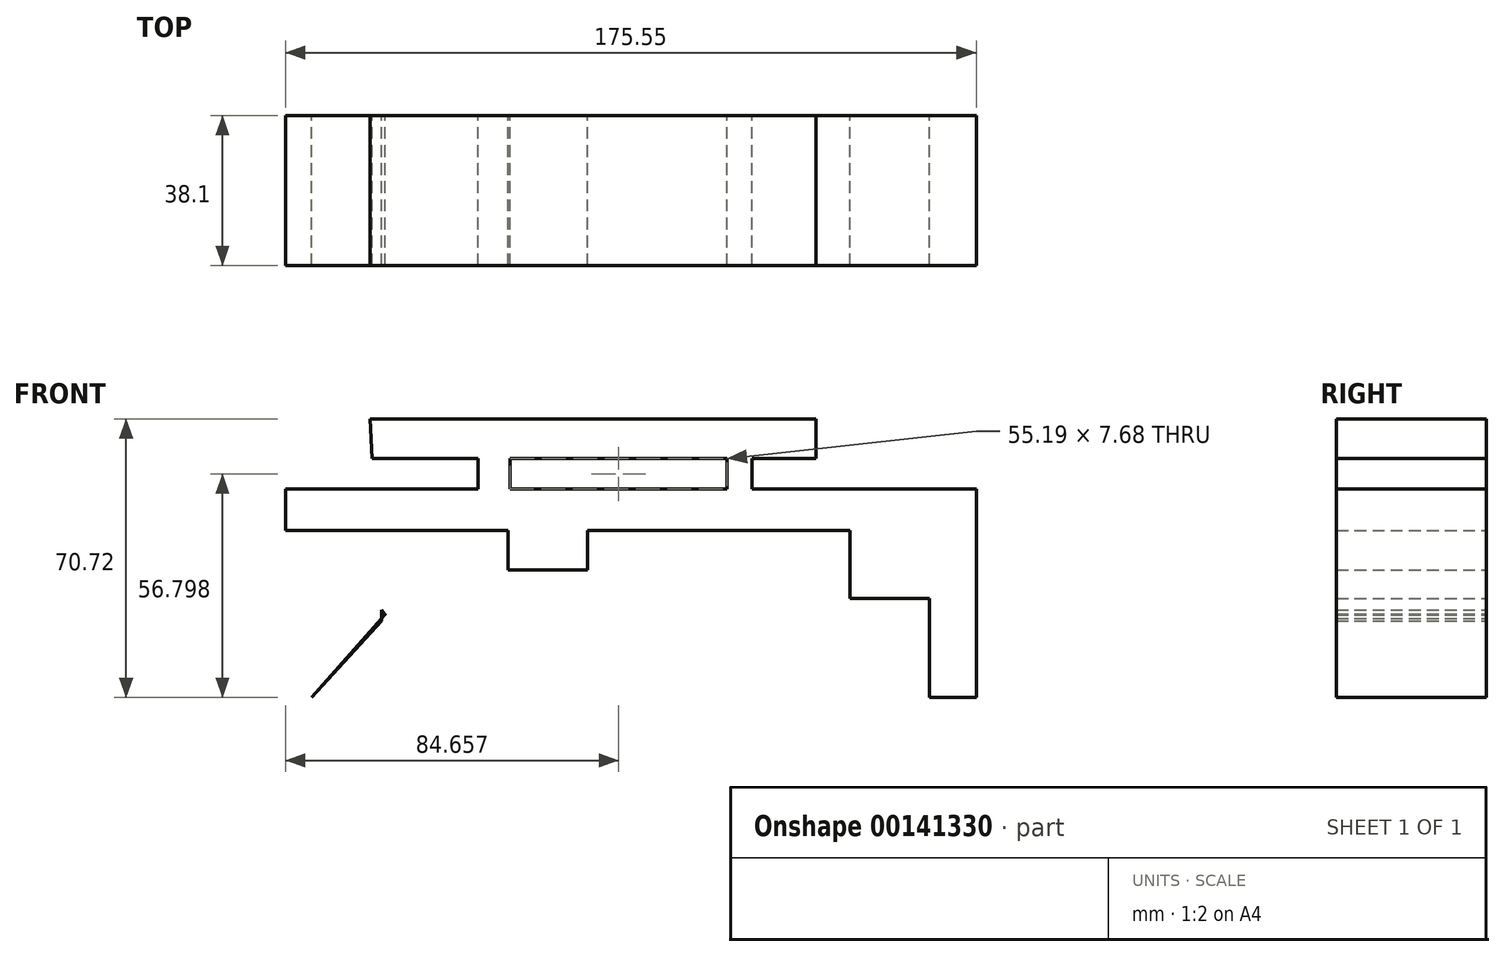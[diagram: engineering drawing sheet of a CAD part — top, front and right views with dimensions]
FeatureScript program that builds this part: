
annotation { "Feature Type Name" : "Feature", "Feature Type Description" : "" }
export const myFeature = defineFeature(function(context is Context, id is Id, definition is map)
    precondition{}
    {
        {
            var Q0;
            Q0=qCreatedBy(makeId("Front.planeOp"),FACE);
            var sketch = newSketch(context, id + "F0", { "sketchPlane" : qUnion([Q0])});
            skLineSegment(sketch, "E0.bottom", {"start": v(0, 42.4) * mm, "end": v(-175.55, 42.4) * mm});
            skLineSegment(sketch, "E0.top", {"start": v(0, 52.96) * mm, "end": v(-175.55, 52.96) * mm});
            skLineSegment(sketch, "E0.left", {"start": v(0, 42.4) * mm, "end": v(0, 52.96) * mm});
            skLineSegment(sketch, "E0.right", {"start": v(-175.55, 42.4) * mm, "end": v(-175.55, 52.96) * mm});
            skPoint(sketch, "E0.middle", {"position": v(-87.77, 47.68) * mm});
            skLineSegment(sketch, "E1", {"start": v(0, 42.4) * mm, "end": v(0, 0) * mm});
            skLineSegment(sketch, "E2", {"start": v(0, 0) * mm, "end": v(-11.94, 0) * mm});
            skLineSegment(sketch, "E3", {"start": v(-11.94, 0) * mm, "end": v(-11.94, 42.4) * mm});
            skLineSegment(sketch, "E4", {"start": v(-118.97, 42.4) * mm, "end": v(-118.97, 32.32) * mm});
            skLineSegment(sketch, "E5", {"start": v(-118.97, 32.32) * mm, "end": v(-98.81, 32.32) * mm});
            skLineSegment(sketch, "E6", {"start": v(-98.81, 32.32) * mm, "end": v(-98.81, 42.4) * mm});
            skLineSegment(sketch, "E7", {"start": v(-118.49, 52.96) * mm, "end": v(-118.49, 60.64) * mm});
            skLineSegment(sketch, "E8", {"start": v(-63.3, 52.96) * mm, "end": v(-63.3, 60.64) * mm});
            skLineSegment(sketch, "E9", {"start": v(-153.53, 60.64) * mm, "end": v(-40.74, 60.64) * mm});
            skLineSegment(sketch, "E10", {"start": v(-40.74, 60.64) * mm, "end": v(-40.74, 70.72) * mm});
            skLineSegment(sketch, "E11", {"start": v(-40.74, 70.72) * mm, "end": v(-154, 70.72) * mm});
            skLineSegment(sketch, "E12", {"start": v(-154, 70.72) * mm, "end": v(-153.53, 60.64) * mm});
            skLineSegment(sketch, "E13", {"start": v(-126.65, 60.64) * mm, "end": v(-126.65, 52.96) * mm});
            skLineSegment(sketch, "E14", {"start": v(-57.06, 60.64) * mm, "end": v(-57.06, 52.96) * mm});
            skLineSegment(sketch, "E15", {"start": v(-32.1, 42.4) * mm, "end": v(-32.1, 25.12) * mm});
            skLineSegment(sketch, "E16", {"start": v(-32.1, 25.12) * mm, "end": v(-11.94, 25.12) * mm});
            skLineSegment(sketch, "E17", {"start": v(-17.22, 42.4) * mm, "end": v(-17.22, 30.88) * mm});
            skLineSegment(sketch, "E18", {"start": v(-17.22, 30.88) * mm, "end": v(-25.86, 31.36) * mm});
            skLineSegment(sketch, "E19", {"start": v(-150.17, 42.4) * mm, "end": v(-150.17, 0) * mm});
            skLineSegment(sketch, "E20", {"start": v(-150.17, 0) * mm, "end": v(-150.17, 21.2) * mm});
            skLineSegment(sketch, "E21", {"start": v(-150.17, 21.2) * mm, "end": v(-168.88, 0) * mm});
            skLineSegment(sketch, "E22", {"start": v(-168.88, 0) * mm, "end": v(-151.13, 19.36) * mm});
            skLineSegment(sketch, "E23", {"start": v(-151.13, 19.36) * mm, "end": v(-151.13, 22.24) * mm});
            skLineSegment(sketch, "E24", {"start": v(-151.13, 22.24) * mm, "end": v(-134.33, 0) * mm});
            skSolve(sketch);
        }
        {
            var Q0;
            Q0 = qSketchRegion(id + "F0", true);
            extrude(context, id + "F1", {"entities" : qUnion([Q0]), "endBound" : BoundingType.SYMMETRIC, "depth" : 38.1 * mm});
        }
    });
